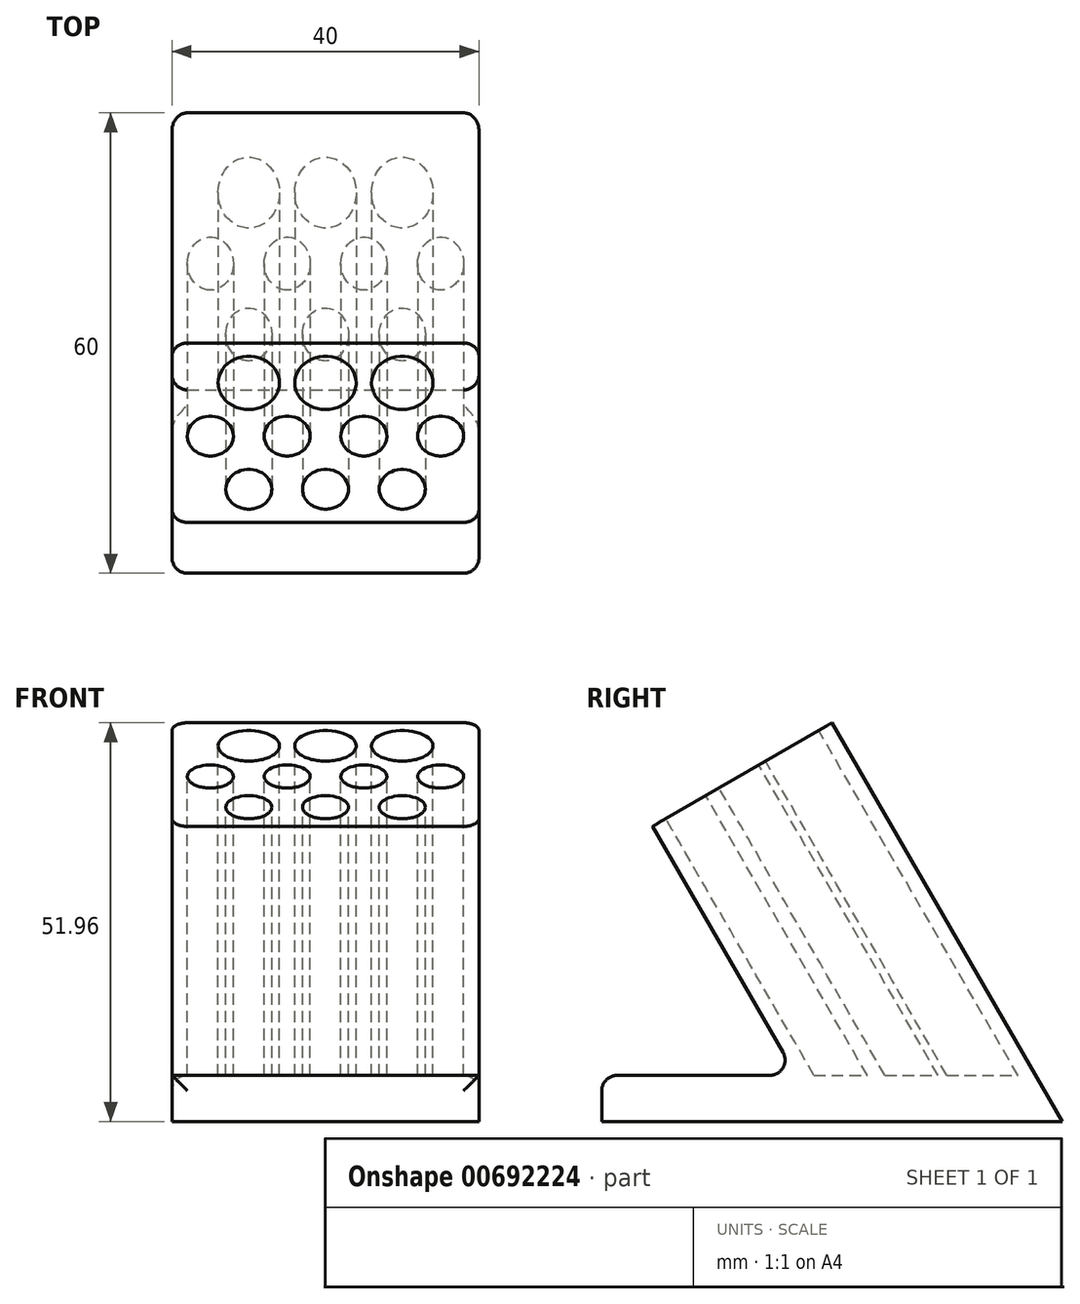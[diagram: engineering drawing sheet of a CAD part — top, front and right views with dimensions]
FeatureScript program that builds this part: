
annotation { "Feature Type Name" : "Feature", "Feature Type Description" : "" }
export const myFeature = defineFeature(function(context is Context, id is Id, definition is map)
    precondition{}
    {
        {
            var Q0;
            Q0=qCreatedBy(makeId("Right.planeOp"),FACE);
            var sketch = newSketch(context, id + "F0", { "sketchPlane" : qUnion([Q0])});
            skLineSegment(sketch, "E0", {"start": v(0, 0) * mm, "end": v(60, 0) * mm});
            skLineSegment(sketch, "E1", {"start": v(60, 0) * mm, "end": v(30, 51.96) * mm});
            skLineSegment(sketch, "E2", {"start": v(30, 51.96) * mm, "end": v(6.62, 38.46) * mm});
            skLineSegment(sketch, "E3", {"start": v(6.62, 38.46) * mm, "end": v(25.36, 6) * mm});
            skLineSegment(sketch, "E4", {"start": v(25.36, 6) * mm, "end": v(0, 6) * mm});
            skLineSegment(sketch, "E5", {"start": v(0, 6) * mm, "end": v(0, 0) * mm});
            skSolve(sketch);
        }
        {
            var Q0;
            Q0=makeQuery(id+"F0.imprint","IMPRINT",FACE,{"disambiguationData":[TD([[makeQuery(id+"F0.imprint","IMPRINT",EDGE,{"derivedFrom":sQuery(id+"F0.wireOp",EDGE,"E0")}),1.0]])]});
            extrude(context, id + "F1", {"entities" : qUnion([Q0]), "depth" : 40 * mm, "offsetDistance" : 25 * mm});
        }
        {
            var Q0;
            Q0=makeQuery(id+"F1.opExtrude","SWEPT_EDGE",EDGE,{"disambiguationData":[OSD([sQuery(id+"F0.wireOp",EDGE,"E3"),sQuery(id+"F0.wireOp",EDGE,"E4")])]});
            var Q1;
            Q1=makeQuery(id+"F1.opExtrude","CAP_EDGE",EDGE,{"disambiguationData":[OSD([sQuery(id+"F0.wireOp",EDGE,"E5")])],"isStart":true});
            var Q2;
            Q2=makeQuery(id+"F1.opExtrude","CAP_EDGE",EDGE,{"disambiguationData":[OSD([sQuery(id+"F0.wireOp",EDGE,"E5")])],"isStart":false});
            var Q3;
            Q3=makeQuery(id+"F1.opExtrude","CAP_EDGE",EDGE,{"disambiguationData":[OSD([sQuery(id+"F0.wireOp",EDGE,"E1")])],"isStart":false});
            var Q4;
            Q4=makeQuery(id+"F1.opExtrude","CAP_EDGE",EDGE,{"disambiguationData":[OSD([sQuery(id+"F0.wireOp",EDGE,"E1")])],"isStart":true});
            var Q5;
            Q5=makeQuery(id+"F1.opExtrude","CAP_EDGE",EDGE,{"disambiguationData":[OSD([sQuery(id+"F0.wireOp",EDGE,"E3")])],"isStart":true});
            var Q6;
            Q6=makeQuery(id+"F1.opExtrude","CAP_EDGE",EDGE,{"disambiguationData":[OSD([sQuery(id+"F0.wireOp",EDGE,"E3")])],"isStart":false});
            var Q7;
            Q7=makeQuery(id+"F1.opExtrude","SWEPT_EDGE",EDGE,{"disambiguationData":[OSD([sQuery(id+"F0.wireOp",EDGE,"E4"),sQuery(id+"F0.wireOp",EDGE,"E5")])]});
            fillet(context, id + "F2", {"entities" : qUnion([Q0, Q1, Q2, Q3, Q4, Q5, Q6, Q7]), "radius" : 2 * mm, "tangentPropagation" : true, "allowEdgeOverflow" : false});
        }
        {
            var Q0;
            Q0=makeQuery(id+"F1.opExtrude","SWEPT_FACE",FACE,{"disambiguationData":[OSD([sQuery(id+"F0.wireOp",EDGE,"E2")])]});
            var sketch = newSketch(context, id + "F3", { "sketchPlane" : qUnion([Q0])});
            skLineSegment(sketch, "E6", {"start": v(0, 51.96) * mm, "end": v(0, 45.96) * mm, "construction": true});
            skLineSegment(sketch, "E7", {"start": v(0, 45.96) * mm, "end": v(10, 45.96) * mm, "construction": true});
            skCircle(sketch, "E8", {"center": v(10, 45.96) * mm, "radius": 4 * mm});
            skCircle(sketch, "E9.1.0.0", {"center": v(20, 45.96) * mm, "radius": 4 * mm});
            skCircle(sketch, "E9.2.0.0", {"center": v(30, 45.96) * mm, "radius": 4 * mm});
            skLineSegment(sketch, "E9.direction1", {"start": v(10, 45.96) * mm, "end": v(20, 45.96) * mm, "construction": true});
            skLineSegment(sketch, "E10", {"start": v(0, 45.96) * mm, "end": v(0, 37.96) * mm, "construction": true});
            skLineSegment(sketch, "E11", {"start": v(0, 37.96) * mm, "end": v(5, 37.96) * mm, "construction": true});
            skCircle(sketch, "E12", {"center": v(5, 37.96) * mm, "radius": 3 * mm});
            skCircle(sketch, "E13.1.0.0", {"center": v(15, 37.96) * mm, "radius": 3 * mm});
            skCircle(sketch, "E13.2.0.0", {"center": v(25, 37.96) * mm, "radius": 3 * mm});
            skCircle(sketch, "E13.3.0.0", {"center": v(35, 37.96) * mm, "radius": 3 * mm});
            skLineSegment(sketch, "E13.direction1", {"start": v(5, 37.96) * mm, "end": v(15, 37.96) * mm, "construction": true});
            skLineSegment(sketch, "E14", {"start": v(10, 37.96) * mm, "end": v(10, 29.96) * mm, "construction": true});
            skCircle(sketch, "E15", {"center": v(10, 29.96) * mm, "radius": 3 * mm});
            skCircle(sketch, "E16.1.0.0", {"center": v(20, 29.96) * mm, "radius": 3 * mm});
            skCircle(sketch, "E16.2.0.0", {"center": v(30, 29.96) * mm, "radius": 3 * mm});
            skLineSegment(sketch, "E16.direction1", {"start": v(10, 29.96) * mm, "end": v(20, 29.96) * mm, "construction": true});
            skSolve(sketch);
        }
        {
            var Q0;
            Q0 = qSketchRegion(id + "F3", true);
            var Q1;
            Q1=makeQuery(id+"F1.opExtrude","SWEPT_FACE",FACE,{"disambiguationData":[OSD([sQuery(id+"F0.wireOp",EDGE,"E4")])]});
            extrude(context, id + "F4", {"entities" : qUnion([Q0]), "operationType" : NewBodyOperationType.REMOVE, "endBound" : BoundingType.UP_TO_SURFACE, "oppositeDirection" : true, "depth" : 25 * mm, "endBoundEntityFace" : qUnion([Q1]), "offsetDistance" : 25 * mm});
        }
    });
